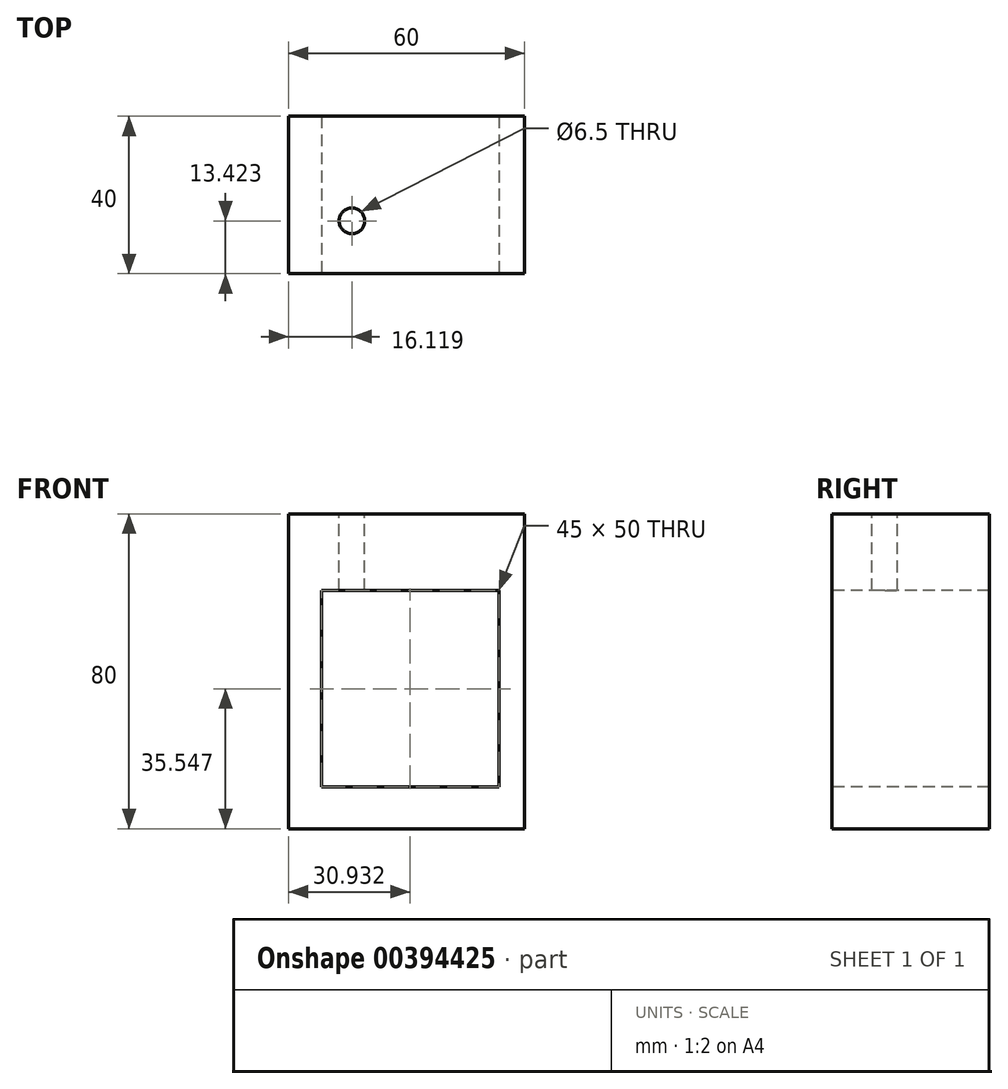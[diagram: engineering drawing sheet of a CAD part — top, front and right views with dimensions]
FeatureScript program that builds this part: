
annotation { "Feature Type Name" : "Feature", "Feature Type Description" : "" }
export const myFeature = defineFeature(function(context is Context, id is Id, definition is map)
    precondition{}
    {
        {
            var Q0;
            Q0=qCreatedBy(makeId("Front.planeOp"),FACE);
            var sketch = newSketch(context, id + "F0", { "sketchPlane" : qUnion([Q0])});
            skLineSegment(sketch, "E0.bottom", {"start": v(0, 0) * mm, "end": v(60, 0) * mm});
            skLineSegment(sketch, "E0.top", {"start": v(0, 80) * mm, "end": v(60, 80) * mm});
            skLineSegment(sketch, "E0.left", {"start": v(0, 0) * mm, "end": v(0, 80) * mm});
            skLineSegment(sketch, "E0.right", {"start": v(60, 0) * mm, "end": v(60, 80) * mm});
            skSolve(sketch);
        }
        {
            var Q0;
            Q0=makeQuery(id+"F0.imprint","IMPRINT",FACE,{"disambiguationData":[TD([[makeQuery(id+"F0.imprint","IMPRINT",EDGE,{"derivedFrom":sQuery(id+"F0.wireOp",EDGE,"E0.bottom")}),1.0]])]});
            extrude(context, id + "F1", {"entities" : qUnion([Q0]), "depth" : 40 * mm});
        }
        {
            var Q0;
            Q0=makeQuery(id+"F1.opExtrude","SWEPT_FACE",FACE,{"disambiguationData":[OSD([sQuery(id+"F0.wireOp",EDGE,"E0.top")])]});
            var sketch = newSketch(context, id + "F2", { "sketchPlane" : qUnion([Q0])});
            skCircle(sketch, "E1", {"center": v(16.12, -26.58) * mm, "radius": 3.25 * mm});
            skSolve(sketch);
        }
        {
            var Q0;
            Q0 = qSketchRegion(id + "F2", true);
            extrude(context, id + "F3", {"entities" : qUnion([Q0]), "operationType" : NewBodyOperationType.REMOVE, "oppositeDirection" : true, "depth" : 25 * mm});
        }
        {
            var Q0;
            Q0=makeQuery(id+"F1.opExtrude","CAP_FACE",FACE,{"disambiguationData":[OSD([sQuery(id+"F0.wireOp",EDGE,"E0.bottom"),sQuery(id+"F0.wireOp",EDGE,"E0.top"),sQuery(id+"F0.wireOp",EDGE,"E0.left"),sQuery(id+"F0.wireOp",EDGE,"E0.right")])],"isStart":false});
            var sketch = newSketch(context, id + "F4", { "sketchPlane" : qUnion([Q0])});
            skLineSegment(sketch, "E2.bottom", {"start": v(8.43, 60.55) * mm, "end": v(53.43, 60.55) * mm});
            skLineSegment(sketch, "E2.top", {"start": v(8.43, 10.55) * mm, "end": v(53.43, 10.55) * mm});
            skLineSegment(sketch, "E2.left", {"start": v(8.43, 60.55) * mm, "end": v(8.43, 10.55) * mm});
            skLineSegment(sketch, "E2.right", {"start": v(53.43, 60.55) * mm, "end": v(53.43, 10.55) * mm});
            skSolve(sketch);
        }
        {
            var Q0;
            Q0=makeQuery(id+"F4.imprint","IMPRINT",FACE,{"disambiguationData":[TD([[makeQuery(id+"F4.imprint","IMPRINT",EDGE,{"derivedFrom":sQuery(id+"F4.wireOp",EDGE,"E2.bottom")}),-1.0]])]});
            extrude(context, id + "F5", {"entities" : qUnion([Q0]), "operationType" : NewBodyOperationType.REMOVE, "endBound" : BoundingType.UP_TO_NEXT, "oppositeDirection" : true, "depth" : 25 * mm});
        }
    });
